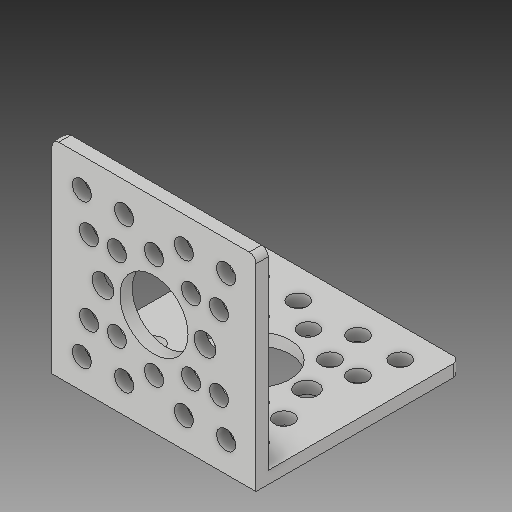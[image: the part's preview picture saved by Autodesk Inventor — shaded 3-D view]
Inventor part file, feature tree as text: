
AUTODESK INVENTOR PART (.ipt)
format: ipt  version: 2017 (Build 210142000, 142)  size: 215,552 bytes
history: native  units: in
note: dims shown in document units (in); Inventor stores cm internally (conversion verified against a paired STEP export)
features: fillet x1
ambient origin geometry x8: Origin, YZ Plane, XZ Plane, XY Plane, X Axis, Y Axis, Z Axis, Center Point
bodies: Solid1 (feature_tree)
feature tree (1):
  fillet  "Fillet1"  [1 undecoded]
note: 1 required parameter value undecoded (feature->parameter linkage not recoverable at this tier; creation-order binding heuristic only, values carry confidence <= 0.55)
